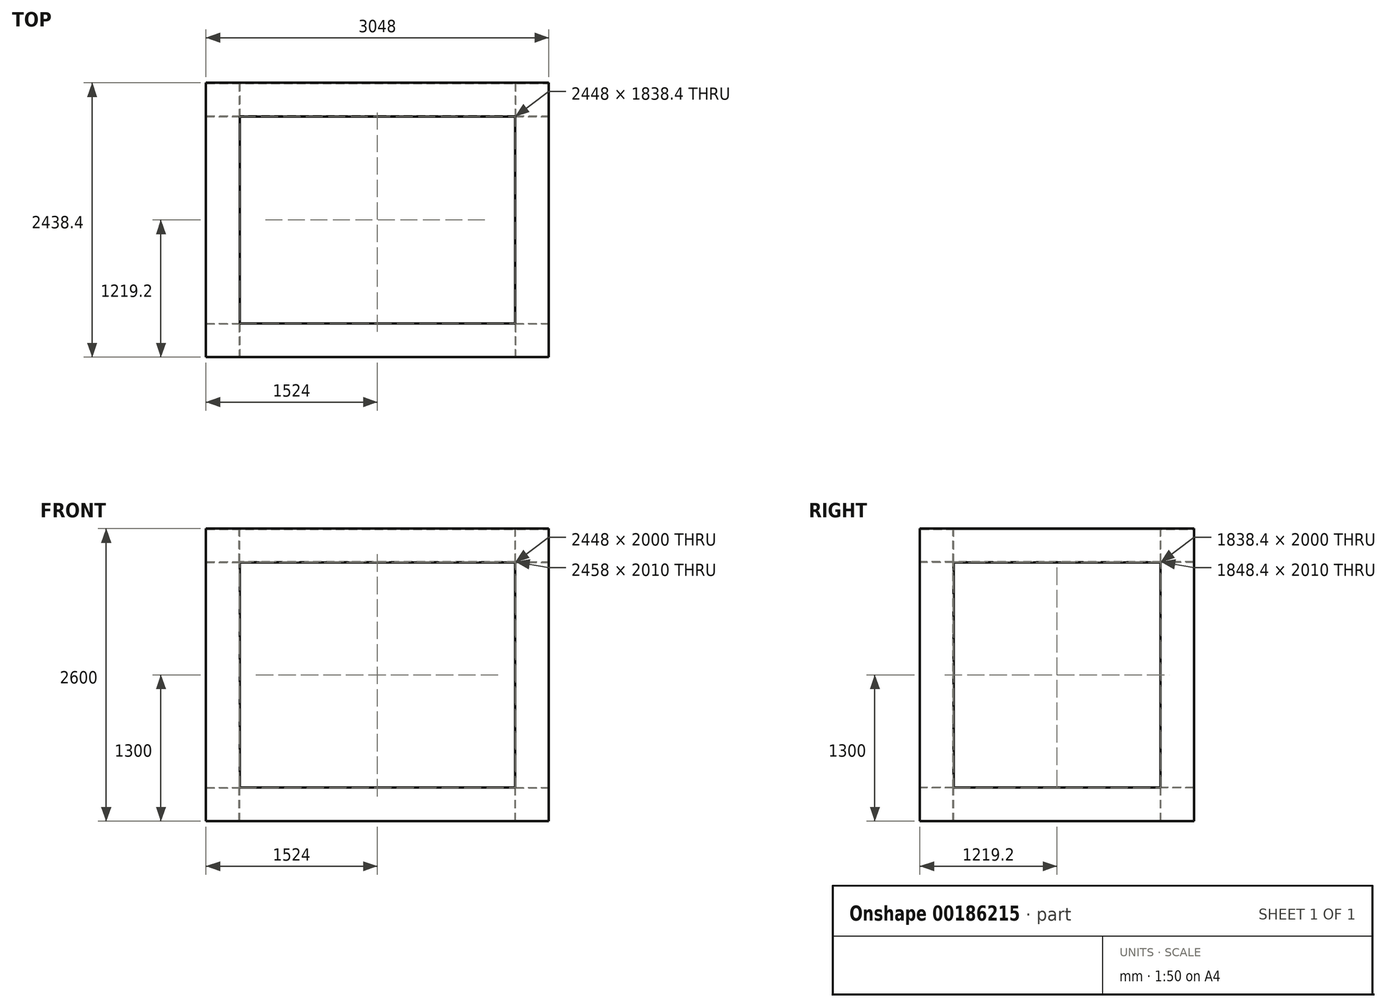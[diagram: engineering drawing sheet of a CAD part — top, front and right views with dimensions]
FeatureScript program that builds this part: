
annotation { "Feature Type Name" : "Feature", "Feature Type Description" : "" }
export const myFeature = defineFeature(function(context is Context, id is Id, definition is map)
    precondition{}
    {
        {
            var Q0;
            Q0=qCreatedBy(makeId("Front.planeOp"),FACE);
            var sketch = newSketch(context, id + "F0", { "sketchPlane" : qUnion([Q0])});
            skLineSegment(sketch, "E0.bottom", {"start": v(0, 0) * mm, "end": v(3048, 0) * mm});
            skLineSegment(sketch, "E0.top", {"start": v(0, 2600) * mm, "end": v(3048, 2600) * mm});
            skLineSegment(sketch, "E0.left", {"start": v(0, 0) * mm, "end": v(0, 2600) * mm});
            skLineSegment(sketch, "E0.right", {"start": v(3048, 0) * mm, "end": v(3048, 2600) * mm});
            skSolve(sketch);
        }
        {
            var Q0;
            Q0 = qSketchRegion(id + "F0", true);
            extrude(context, id + "F1", {"entities" : qUnion([Q0]), "depth" : 2438.4 * mm});
        }
        {
            var Q0;
            Q0=makeQuery(id+"F1.opExtrude","CAP_FACE",FACE,{"disambiguationData":[OSD([sQuery(id+"F0.wireOp",EDGE,"E0.bottom"),sQuery(id+"F0.wireOp",EDGE,"E0.top"),sQuery(id+"F0.wireOp",EDGE,"E0.left"),sQuery(id+"F0.wireOp",EDGE,"E0.right")])],"isStart":false});
            var sketch = newSketch(context, id + "F2", { "sketchPlane" : qUnion([Q0])});
            skLineSegment(sketch, "E1.0.0", {"start": v(0, 2600) * mm, "end": v(0, 0) * mm});
            skLineSegment(sketch, "E1.0.1", {"start": v(0, 0) * mm, "end": v(3048, 0) * mm});
            skLineSegment(sketch, "E1.0.2", {"start": v(3048, 0) * mm, "end": v(3048, 2600) * mm});
            skLineSegment(sketch, "E1.0.3", {"start": v(3048, 2600) * mm, "end": v(0, 2600) * mm});
            skLineSegment(sketch, "E2.0", {"start": v(2748, 2300) * mm, "end": v(300, 2300) * mm});
            skLineSegment(sketch, "E2.1", {"start": v(2748, 300) * mm, "end": v(2748, 2300) * mm});
            skLineSegment(sketch, "E2.2", {"start": v(300, 300) * mm, "end": v(2748, 300) * mm});
            skLineSegment(sketch, "E2.3", {"start": v(300, 2300) * mm, "end": v(300, 300) * mm});
            skSolve(sketch);
        }
        {
            var Q0;
            Q0=makeQuery(id+"F2.imprint","IMPRINT",FACE,{"disambiguationData":[TD([[makeQuery(id+"F2.imprint","IMPRINT",EDGE,{"derivedFrom":sQuery(id+"F2.wireOp",EDGE,"E2.0")}),1.0]])]});
            extrude(context, id + "F3", {"entities" : qUnion([Q0]), "operationType" : NewBodyOperationType.REMOVE, "oppositeDirection" : true, "depth" : 3920 * mm});
        }
        {
            var Q0;
            Q0=makeQuery(id+"F1.opExtrude","SWEPT_FACE",FACE,{"disambiguationData":[OSD([sQuery(id+"F0.wireOp",EDGE,"E0.right")])]});
            var sketch = newSketch(context, id + "F4", { "sketchPlane" : qUnion([Q0])});
            skLineSegment(sketch, "E3.0", {"start": v(-300, 300) * mm, "end": v(-300, 2300) * mm});
            skLineSegment(sketch, "E3.1", {"start": v(-2138.4, 300) * mm, "end": v(-300, 300) * mm});
            skLineSegment(sketch, "E3.2", {"start": v(-2138.4, 2300) * mm, "end": v(-2138.4, 300) * mm});
            skLineSegment(sketch, "E3.3", {"start": v(-300, 2300) * mm, "end": v(-2138.4, 2300) * mm});
            skSolve(sketch);
        }
        {
            var Q0;
            Q0 = qSketchRegion(id + "F4", true);
            extrude(context, id + "F5", {"entities" : qUnion([Q0]), "operationType" : NewBodyOperationType.REMOVE, "oppositeDirection" : true, "depth" : 4630 * mm});
        }
        {
            var Q0;
            Q0=makeQuery(id+"F1.opExtrude","SWEPT_FACE",FACE,{"disambiguationData":[OSD([sQuery(id+"F0.wireOp",EDGE,"E0.top")])]});
            var sketch = newSketch(context, id + "F6", { "sketchPlane" : qUnion([Q0])});
            skLineSegment(sketch, "E4.0", {"start": v(2748, -300) * mm, "end": v(300, -300) * mm});
            skLineSegment(sketch, "E4.1", {"start": v(2748, -2138.4) * mm, "end": v(2748, -300) * mm});
            skLineSegment(sketch, "E4.2", {"start": v(300, -2138.4) * mm, "end": v(2748, -2138.4) * mm});
            skLineSegment(sketch, "E4.3", {"start": v(300, -300) * mm, "end": v(300, -2138.4) * mm});
            skLineSegment(sketch, "E5.0", {"start": v(3043, -5) * mm, "end": v(5, -5) * mm});
            skLineSegment(sketch, "E5.1", {"start": v(3043, -2433.4) * mm, "end": v(3043, -5) * mm});
            skLineSegment(sketch, "E5.2", {"start": v(5, -2433.4) * mm, "end": v(3043, -2433.4) * mm});
            skLineSegment(sketch, "E5.3", {"start": v(5, -5) * mm, "end": v(5, -2433.4) * mm});
            skSolve(sketch);
        }
        {
            var Q0;
            Q0=makeQuery(id+"F6.imprint","IMPRINT",FACE,{"disambiguationData":[TD([[makeQuery(id+"F6.imprint","IMPRINT",EDGE,{"derivedFrom":sQuery(id+"F6.wireOp",EDGE,"E4.0")}),1.0]])]});
            extrude(context, id + "F7", {"entities" : qUnion([Q0]), "operationType" : NewBodyOperationType.REMOVE, "oppositeDirection" : true, "depth" : 3030 * mm});
        }
        {
            var Q0;
            Q0=makeQuery(id+"F1.opExtrude","SWEPT_FACE",FACE,{"disambiguationData":[OSD([sQuery(id+"F0.wireOp",EDGE,"E0.bottom")])]});
            shell(context, id + "F8", {"entities" : qUnion([Q0]), "thickness" : 5 * mm});
        }
    });
